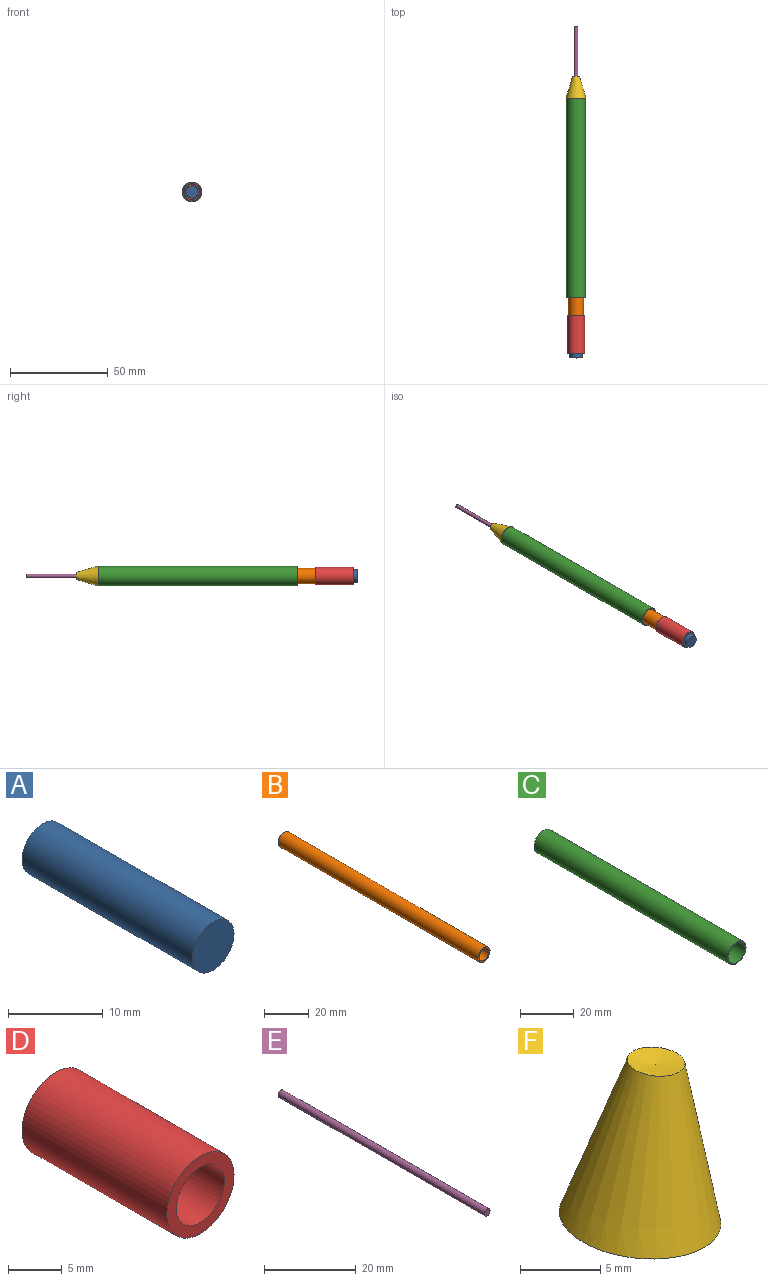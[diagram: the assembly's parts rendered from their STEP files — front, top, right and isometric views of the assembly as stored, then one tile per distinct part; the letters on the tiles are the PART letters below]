
ASSEMBLY  parts=6 mates=5
PART A: 3 faces, bbox 6.2x25.4x6.2 mm
  f0: cylinder r=3.11mm len=25.4mm, axis (0,1,0), area 496.3mm2, adj f1,f2
  f1: plane 6.22x6.22mm, normal (0,-1,0), area 30.4mm2, adj f0
  f2: plane 6.22x6.22mm, normal (0,1,0), area 30.4mm2, adj f0
PART B: 4 faces, bbox 7.7x127x7.7 mm
  f0: plane 7.74x7.74mm, normal (0,1,0), area 16.7mm2, adj f2,f3
  f1: plane 7.74x7.74mm, normal (0,-1,0), area 16.7mm2, adj f2,f3
  f2: cylinder r=3.87mm len=127mm, axis (0,-1,0), area 3089.6mm2, adj f0,f1
  f3: cylinder r=3.11mm len=127mm, axis (0,-1,0), area 2481.6mm2, adj f0,f1
PART C: 4 faces, bbox 9.8x101.6x9.8 mm
  f0: plane 9.79x9.79mm, normal (0,1,0), area 14.8mm2, adj f2,f3
  f1: plane 9.79x9.79mm, normal (0,-1,0), area 14.8mm2, adj f2,f3
  f2: cylinder r=4.89mm len=101.6mm, axis (0,-1,0), area 3124.6mm2, adj f0,f1
  f3: cylinder r=4.39mm len=101.6mm, axis (0,-1,0), area 2800.3mm2, adj f0,f1
PART D: 4 faces, bbox 8.8x19.1x8.8 mm
  f0: plane 8.84x8.84mm, normal (0,1,0), area 30.2mm2, adj f2,f3
  f1: plane 8.84x8.84mm, normal (0,-1,0), area 30.2mm2, adj f2,f3
  f2: cylinder r=4.42mm len=19.05mm, axis (0,-1,0), area 528.9mm2, adj f0,f1
  f3: cylinder r=3.15mm len=19.05mm, axis (0,-1,0), area 376.9mm2, adj f0,f1
PART E: 3 faces, bbox 1.8x63.5x1.8 mm
  f0: cylinder r=0.89mm len=63.5mm, axis (0,1,0), area 356.6mm2, adj f1,f2
  f1: plane 1.79x1.79mm, normal (0,-1,0), area 2.5mm2, adj f0
  f2: plane 1.79x1.79mm, normal (0,1,0), area 2.5mm2, adj f0
PART F: 3 faces, bbox 10x10.1x12 mm
  f0: cone r=0mm half-angle=82.7deg, axis (0.13,0,0.99), area 10.2mm2, adj f2
  f1: cone r=5.04mm half-angle=82.7deg, axis (0.13,0,0.99), area 80.4mm2, adj f2
  f2: cone r=1.79mm half-angle=16.1deg, axis (-0.13,0,-0.99), area 251.6mm2, adj f0,f1
PLACE A rot(axis=(0.07,1,0.05),0deg) t=(290.97,-54.96,39.05)mm
PLACE B rot(axis=(0.07,1,0.05),0deg) t=(294.05,49.18,71.94)mm
PLACE C rot(axis=(0.07,1,0.05),0deg) t=(294.05,52.36,71.94)mm
PLACE D rot(axis=(0.07,1,0.05),0deg) t=(280.56,-58.77,25.62)mm
PLACE E rot(axis=(0.07,1,0.05),0deg) t=(287.42,89.19,47.79)mm
PLACE F rot(axis=(-0.6,-0.6,-0.53),124.3deg) t=(294.05,55.8,73.81)mm
MATE slider A.f0 <-> B.f2  axis (0,-1,0) through (294.05,-80.36,71.94)mm
MATE fastened D.f2 <-> B.f2  axis (0,-1,0) through (294.05,-77.82,71.94)mm
MATE slider E.f0 <-> F.f0  axis (0,1,0) through (294.05,57.44,71.94)mm
MATE fastened F.f0 <-> C.f2  axis (0,-1,0) through (294.05,52.36,71.94)mm
MATE slider D.f2 <-> C.f2  axis (0,1,0) through (294.05,-58.77,71.94)mm
